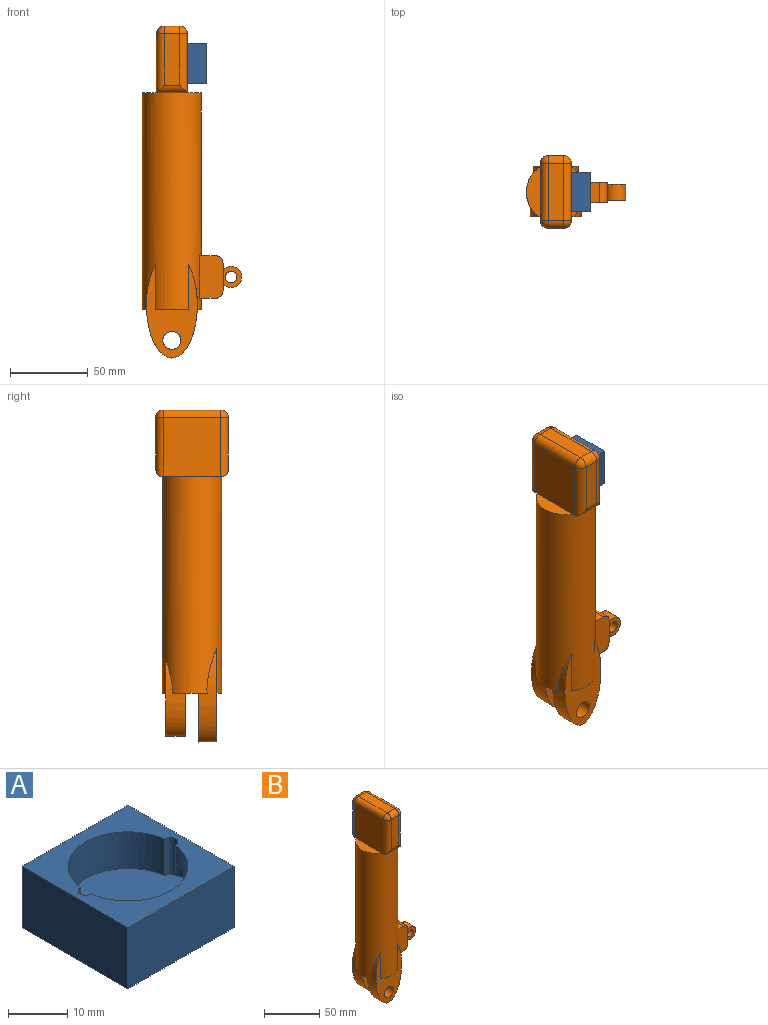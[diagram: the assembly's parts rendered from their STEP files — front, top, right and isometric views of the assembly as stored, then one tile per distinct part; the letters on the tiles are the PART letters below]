
ASSEMBLY  parts=2 mates=1
PART A: 16 faces, bbox 25.4x25.4x12.7 mm
  f0: cylinder r=10.16mm len=20.16mm, axis (0,0,1), area 212.7mm2, adj f1,f7,f9,f10,f11,f13,f14,f15
  f1: cylinder r=1.27mm len=7.62mm, axis (0,0,1), area 23.8mm2, adj f0,f2,f7,f10,f14,f15
  f2: cylinder r=10.16mm len=20.16mm, axis (0,0,1), area 215.7mm2, adj f1,f7,f9,f10,f12,f13
  f3: plane 25.4x12.7mm, normal (0,-1,0), area 322.6mm2, adj f4,f6,f7,f8
  f4: plane 25.4x12.7mm, normal (1,0,0), area 322.6mm2, adj f3,f5,f7,f8
  f5: plane 25.4x12.7mm, normal (0,1,0), area 322.6mm2, adj f4,f6,f7,f8
  f6: plane 25.4x12.7mm, normal (-1,0,0), area 322.6mm2, adj f3,f5,f7,f8
  f7: plane 25.4x25.4mm, normal (0,0,1), area 315.7mm2, adj f0,f1,f2,f3,f4,f5,f6,f9
  f8: plane 25.4x25.4mm, normal (0,0,-1), area 645.2mm2, adj f3,f4,f5,f6
  f9: cylinder r=1.27mm len=3.81mm, axis (0,0,1), area 15.8mm2, adj f0,f2,f7,f11,f12
  f10: plane 23.5x20.32mm, normal (0,0,1), area 337.1mm2, adj f0,f1,f2,f13,f15
  f11: plane 1.07x0.71mm, normal (0,0,-1), area 0.1mm2, adj f0,f9,f13
  f12: plane 4.2x2.16mm, normal (0,0,-1), area 3.4mm2, adj f2,f9,f13
  f13: cylinder r=2.54mm len=4.91mm, axis (0,0,-1), area 25.7mm2, adj f0,f2,f10,f11,f12
  f14: plane 3.77x2.33mm, normal (0,0,-1), area 4.2mm2, adj f0,f1,f15
  f15: cylinder r=2.54mm len=3.81mm, axis (0,0,-1), area 19.3mm2, adj f0,f1,f10,f14
PART B: 53 faces, bbox 64.1x47x214.2 mm
  f0: plane 38.1x36.82mm, normal (1,0,0), area 757.8mm2, adj f1,f3,f28,f34,f38,f43,f48,f49
  f1: plane 5.04x2.16mm, normal (0,0,-1), area 4.7mm2, adj f0,f5,f40
  f2: plane 5.04x2.16mm, normal (0,0,-1), area 4.7mm2, adj f5,f31,f36
  f3: plane 32.51x9.12mm, normal (0,0,1), area 209.5mm2, adj f0,f5
  f4: plane 17.22x2.06mm, normal (0,0,-1), area 23.9mm2, adj f5,f24
  f5: cylinder r=19.05mm len=139.7mm, axis (0,0,-1), area 15801.5mm2, adj f1,f2,f3,f4,f6,f7,f8,f9
  f6: plane 38.1x22.33mm, normal (0,0,-1), area 380.5mm2, adj f5,f20,f22,f23,f25
  f7: plane 32.51x9.12mm, normal (0,0,1), area 209.5mm2, adj f5,f31
  f8: plane 21.51x3.33mm, normal (0,0,-1), area 48.6mm2, adj f5,f21
  f9: plane 27.6x15.13mm, normal (0,-1,0), area 406.5mm2, adj f5,f11,f12,f13,f18,f19
  f10: plane 27.6x15.13mm, normal (0,1,0), area 406.5mm2, adj f5,f11,f12,f13,f18,f19
  f11: plane 13.1x10.05mm, normal (0,0,1), area 121.5mm2, adj f5,f9,f10,f19
  f12: plane 13.1x10.05mm, normal (0,0,-1), area 121.5mm2, adj f5,f9,f10,f18
  f13: plane 17.44x13.1mm, normal (1,0,0), area 138.6mm2, adj f9,f10,f15,f16,f17,f18,f19
  f14: cylinder r=3.74mm len=10.16mm, axis (0,1,0), area 238.8mm2, adj f16,f17
  f15: cylinder r=6.81mm len=13.62mm, axis (0,1,0), area 337.2mm2, adj f13,f16,f17
  f16: plane 13.62x12mm, normal (0,-1,0), area 92mm2, adj f13,f14,f15
  f17: plane 13.62x12mm, normal (0,1,0), area 92mm2, adj f13,f14,f15
  f18: cylinder r=5.08mm len=13.1mm, axis (0,-1,0), area 104.5mm2, adj f9,f10,f12,f13
  f19: cylinder r=5.08mm len=13.1mm, axis (0,1,0), area 104.5mm2, adj f9,f10,f11,f13
  f20: extruded ~60.09x32.81mm, area 1108.5mm2, adj f5,f6,f21,f22
  f21: plane 60.09x32.85mm, normal (0,-1,0), area 917mm2, adj f5,f8,f20,f27
  f22: plane 32.74x31.32mm, normal (0,1,0), area 680.7mm2, adj f6,f20,f27
  f23: extruded ~49.4x28.61mm, area 982.2mm2, adj f5,f6,f24,f25
  f24: plane 49.4x28.61mm, normal (0,1,0), area 684.6mm2, adj f4,f5,f23,f26
  f25: plane 28.61x27.47mm, normal (0,-1,0), area 510mm2, adj f6,f23,f26
  f26: cylinder r=5.84mm len=12.7mm, axis (0,1,0), area 466.2mm2, adj f24,f25
  f27: cylinder r=5.84mm len=11.68mm, axis (0,1,0), area 419.6mm2, adj f21,f22
  f28: plane 5.04x2.16mm, normal (0,0,-1), area 4.7mm2, adj f0,f5,f36
  f29: plane 5.04x2.16mm, normal (0,0,-1), area 4.7mm2, adj f5,f31,f40
  f30: plane 33.02x9.71mm, normal (0,1,0), area 320.5mm2, adj f34,f35,f36,f37
  f31: plane 38.1x36.82mm, normal (-1,0,0), area 1403mm2, adj f2,f7,f29,f37,f41,f46
  f32: plane 33.02x9.71mm, normal (0,-1,0), area 320.5mm2, adj f38,f39,f40,f41
  f33: plane 36.82x9.71mm, normal (0,0,1), area 357.4mm2, adj f35,f39,f43,f46
  f34: cylinder r=5.08mm len=38.1mm, axis (0,0,-1), area 289.3mm2, adj f0,f30,f36,f44
  f35: cylinder r=5.08mm len=9.71mm, axis (1,0,0), area 77.4mm2, adj f30,f33,f44,f47
  f36: cylinder r=5.08mm len=19.87mm, axis (-1,0,0), area 124.9mm2, adj f2,f5,f28,f30,f34,f37
  f37: cylinder r=5.08mm len=38.1mm, axis (0,0,1), area 289.3mm2, adj f30,f31,f36,f47
  f38: cylinder r=5.08mm len=38.1mm, axis (0,0,1), area 289.3mm2, adj f0,f32,f40,f42
  f39: cylinder r=5.08mm len=9.71mm, axis (-1,0,0), area 77.4mm2, adj f32,f33,f42,f45
  f40: cylinder r=5.08mm len=19.87mm, axis (1,0,0), area 124.9mm2, adj f1,f5,f29,f32,f38,f41
  f41: cylinder r=5.08mm len=38.1mm, axis (0,0,-1), area 289.3mm2, adj f31,f32,f40,f45
  f42: sphere r=5.08mm, area 40.5mm2, adj f38,f39,f43
  f43: cylinder r=5.08mm len=36.82mm, axis (0,-1,0), area 293.8mm2, adj f0,f33,f42,f44
  f44: sphere r=5.08mm, area 40.5mm2, adj f34,f35,f43
  f45: sphere r=5.08mm, area 40.5mm2, adj f39,f41,f46
  f46: cylinder r=5.08mm len=36.82mm, axis (0,1,0), area 293.8mm2, adj f31,f33,f45,f47
  f47: sphere r=5.08mm, area 40.5mm2, adj f35,f37,f46
  f48: plane 25.4x7.62mm, normal (0,-1,0), area 193.5mm2, adj f0,f49,f51,f52
  f49: plane 25.4x7.62mm, normal (0,0,-1), area 193.5mm2, adj f0,f48,f50,f52
  f50: plane 25.4x7.62mm, normal (0,1,0), area 193.5mm2, adj f0,f49,f51,f52
  f51: plane 25.4x7.62mm, normal (0,0,1), area 193.5mm2, adj f0,f48,f50,f52
  f52: plane 25.4x25.4mm, normal (1,0,0), area 645.2mm2, adj f48,f49,f50,f51
PLACE A rot(axis=(0.71,0,0.71),180deg) t=(7.61,37.81,130.46)mm
PLACE B t=(-2.32,37.81,-28.29)mm
MATE fastened A.f0 <-> B.f0  axis (-1,0,0) through (7.61,37.81,130.46)mm
